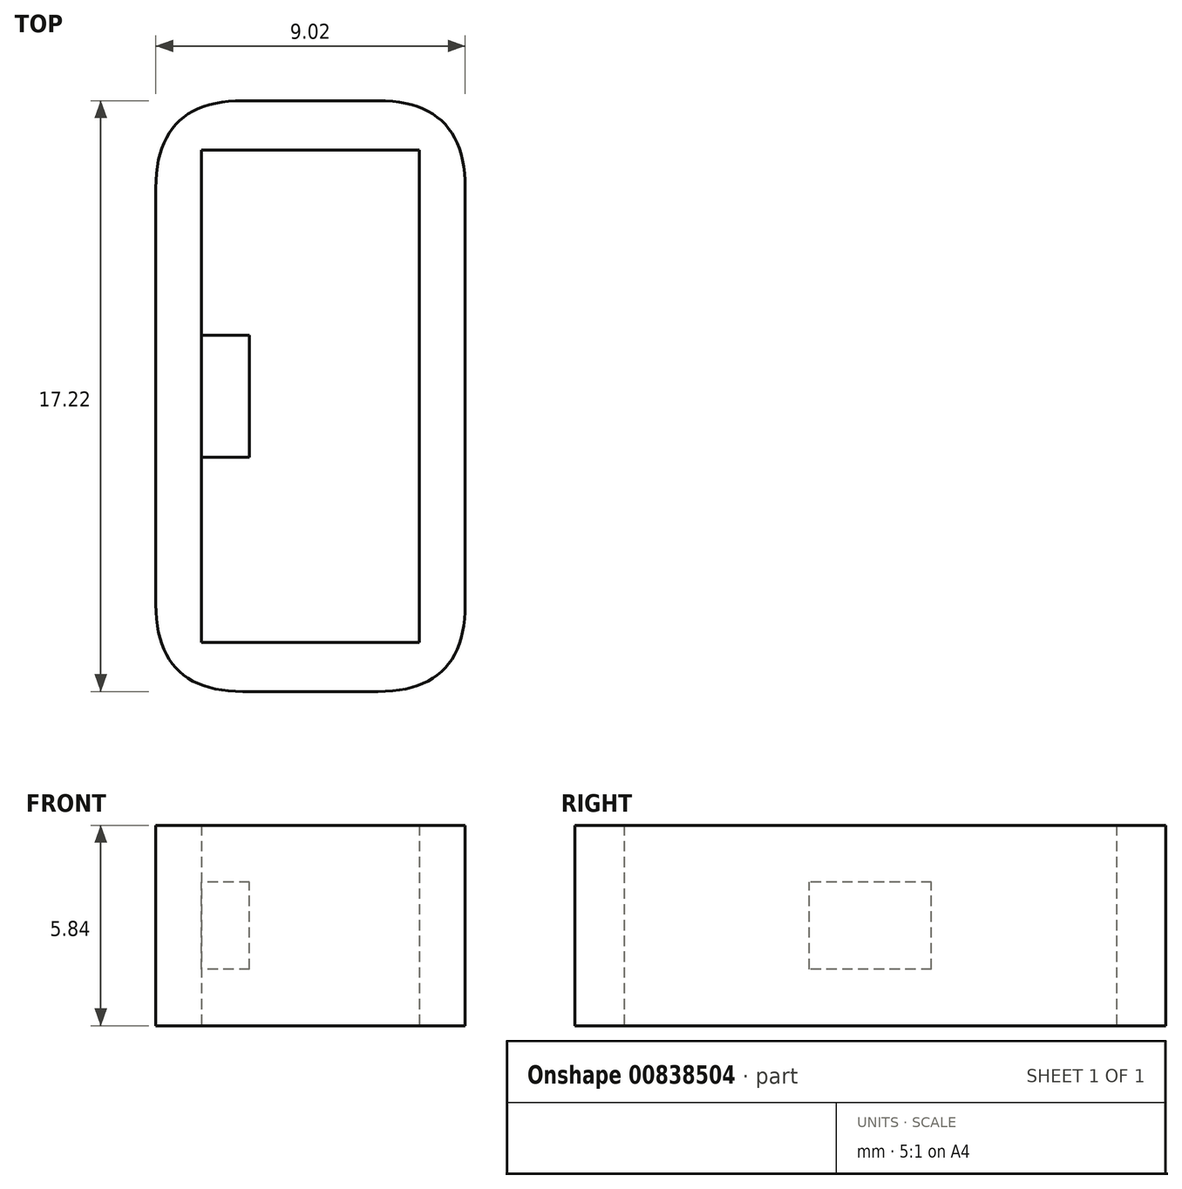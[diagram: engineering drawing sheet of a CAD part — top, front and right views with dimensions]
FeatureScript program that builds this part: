
annotation { "Feature Type Name" : "Feature", "Feature Type Description" : "" }
export const myFeature = defineFeature(function(context is Context, id is Id, definition is map)
    precondition{}
    {
        {
            var Q0;
            Q0=qCreatedBy(makeId("Top.planeOp"),FACE);
            var sketch = newSketch(context, id + "F0", { "sketchPlane" : qUnion([Q0])});
            skLineSegment(sketch, "E0.bottom", {"start": v(4.5, -8.61) * mm, "end": v(-4.5, -8.61) * mm});
            skLineSegment(sketch, "E0.top", {"start": v(4.5, 8.61) * mm, "end": v(-4.5, 8.61) * mm});
            skLineSegment(sketch, "E0.left", {"start": v(4.5, -8.61) * mm, "end": v(4.5, 8.61) * mm});
            skLineSegment(sketch, "E0.right", {"start": v(-4.5, -8.61) * mm, "end": v(-4.5, 8.61) * mm});
            skPoint(sketch, "E0.middle", {"position": v(0, 0) * mm});
            skLineSegment(sketch, "E1.bottom", {"start": v(3.18, -7.18) * mm, "end": v(-3.18, -7.18) * mm});
            skLineSegment(sketch, "E1.top", {"start": v(3.18, 7.18) * mm, "end": v(-3.17, 7.18) * mm});
            skLineSegment(sketch, "E1.left", {"start": v(3.18, -7.18) * mm, "end": v(3.18, 7.18) * mm});
            skLineSegment(sketch, "E1.right", {"start": v(-3.18, -7.18) * mm, "end": v(-3.17, 7.18) * mm});
            skSolve(sketch);
        }
        {
            var Q0;
            Q0 = qSketchRegion(id + "F0", true);
            extrude(context, id + "F1", {"entities" : qUnion([Q0]), "depth" : 5.84 * mm, "offsetDistance" : 25.4 * mm});
        }
        {
            var Q0;
            Q0=makeQuery(id+"F1.opExtrude","SWEPT_EDGE",EDGE,{"disambiguationData":[OSD([sQuery(id+"F0.wireOp",EDGE,"E0.top"),sQuery(id+"F0.wireOp",EDGE,"E0.right")])]});
            var Q1;
            Q1=makeQuery(id+"F1.opExtrude","SWEPT_EDGE",EDGE,{"disambiguationData":[OSD([sQuery(id+"F0.wireOp",EDGE,"E0.bottom"),sQuery(id+"F0.wireOp",EDGE,"E0.right")])]});
            var Q2;
            Q2=makeQuery(id+"F1.opExtrude","SWEPT_EDGE",EDGE,{"disambiguationData":[OSD([sQuery(id+"F0.wireOp",EDGE,"E0.bottom"),sQuery(id+"F0.wireOp",EDGE,"E0.left")])]});
            var Q3;
            Q3=makeQuery(id+"F1.opExtrude","SWEPT_EDGE",EDGE,{"disambiguationData":[OSD([sQuery(id+"F0.wireOp",EDGE,"E0.top"),sQuery(id+"F0.wireOp",EDGE,"E0.left")])]});
            fillet(context, id + "F2", {"entities" : qUnion([Q0, Q1, Q2, Q3]), "radius" : 2.54 * mm, "tangentPropagation" : true, "rho" : 0.5, "crossSection" : FilletCrossSection.CONIC, "allowEdgeOverflow" : false});
        }
        {
            var Q0;
            Q0=makeQuery(id+"F1.opExtrude","SWEPT_FACE",FACE,{"disambiguationData":[OSD([sQuery(id+"F0.wireOp",EDGE,"E1.right")])]});
            var sketch = newSketch(context, id + "F3", { "sketchPlane" : qUnion([Q0])});
            skLineSegment(sketch, "E2.bottom", {"start": v(1.78, 1.65) * mm, "end": v(-1.78, 1.65) * mm});
            skLineSegment(sketch, "E2.top", {"start": v(1.78, 4.2) * mm, "end": v(-1.78, 4.2) * mm});
            skLineSegment(sketch, "E2.left", {"start": v(1.78, 1.65) * mm, "end": v(1.78, 4.2) * mm});
            skLineSegment(sketch, "E2.right", {"start": v(-1.78, 1.65) * mm, "end": v(-1.78, 4.2) * mm});
            skPoint(sketch, "E2.middle", {"position": v(0, 2.92) * mm});
            skPoint(sketch, "E2.middle.positionSnap0", {"position": v(-7.18, 2.92) * mm});
            skPoint(sketch, "E2.middle.positionSnap1", {"position": v(0, 5.84) * mm});
            skPoint(sketch, "E2.centerSnap0", {"position": v(-7.18, 2.92) * mm});
            skPoint(sketch, "E2.centerSnap1", {"position": v(0, 5.84) * mm});
            skSolve(sketch);
        }
        {
            var Q0;
            Q0 = qSketchRegion(id + "F3", true);
            extrude(context, id + "F4", {"entities" : qUnion([Q0]), "depth" : 1.4 * mm, "offsetDistance" : 25.4 * mm});
        }
    });
